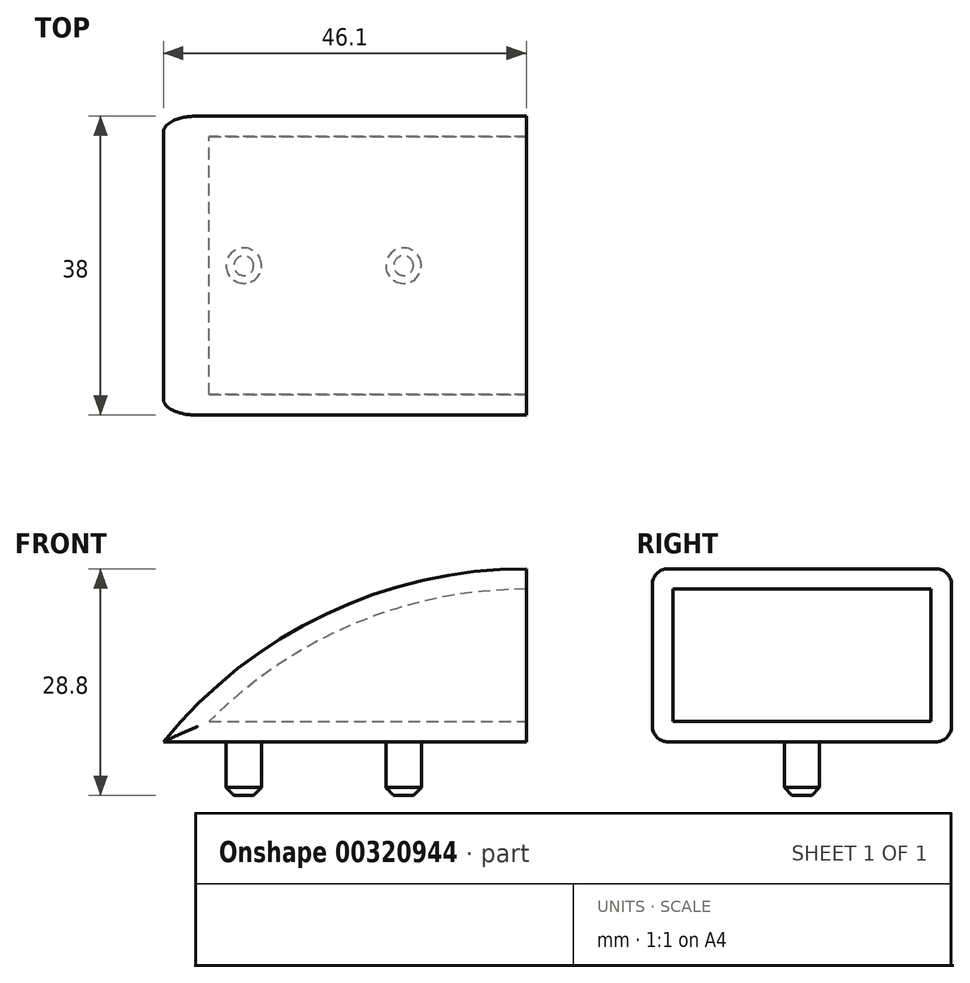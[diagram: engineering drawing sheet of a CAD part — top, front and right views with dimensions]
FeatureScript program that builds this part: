
annotation { "Feature Type Name" : "Feature", "Feature Type Description" : "" }
export const myFeature = defineFeature(function(context is Context, id is Id, definition is map)
    precondition{}
    {
        {
            var Q0;
            Q0=qCreatedBy(makeId("Front.planeOp"),FACE);
            var sketch = newSketch(context, id + "F0", { "sketchPlane" : qUnion([Q0])});
            skLineSegment(sketch, "E0", {"start": v(0, 0) * mm, "end": v(46.1, 0) * mm});
            skLineSegment(sketch, "E1", {"start": v(46.1, 0) * mm, "end": v(46.1, 22) * mm});
            skArc(sketch, "E2", {"start": v(46.1, 22) * mm, "mid": v(20.56, 16.22) * mm, "end": v(0, 0) * mm});
            skSolve(sketch);
        }
        {
            var Q0;
            Q0 = qSketchRegion(id + "F0", true);
            extrude(context, id + "F1", {"entities" : qUnion([Q0]), "depth" : 38 * mm});
        }
        {
            var Q0;
            Q0=makeQuery(id+"F1.opExtrude","SWEPT_FACE",FACE,{"disambiguationData":[OSD([sQuery(id+"F0.wireOp",EDGE,"E1")])]});
            shell(context, id + "F2", {"entities" : qUnion([Q0]), "thickness" : 2.6 * mm});
        }
        {
            var Q0;
            Q0=makeQuery(id+"F1.opExtrude","CAP_EDGE",EDGE,{"disambiguationData":[OSD([sQuery(id+"F0.wireOp",EDGE,"E2")])],"isStart":false});
            var Q1;
            Q1=makeQuery(id+"F1.opExtrude","CAP_EDGE",EDGE,{"disambiguationData":[OSD([sQuery(id+"F0.wireOp",EDGE,"E2")])],"isStart":true});
            var Q2;
            Q2=makeQuery(id+"F1.opExtrude","CAP_EDGE",EDGE,{"disambiguationData":[OSD([sQuery(id+"F0.wireOp",EDGE,"E0")])],"isStart":true});
            var Q3;
            Q3=makeQuery(id+"F1.opExtrude","CAP_EDGE",EDGE,{"disambiguationData":[OSD([sQuery(id+"F0.wireOp",EDGE,"E0")])],"isStart":false});
            fillet(context, id + "F3", {"entities" : qUnion([Q0, Q1, Q2, Q3]), "radius" : 2 * mm, "tangentPropagation" : true, "allowEdgeOverflow" : false});
        }
        {
            var Q0;
            Q0=makeQuery(id+"F1.opExtrude","SWEPT_FACE",FACE,{"disambiguationData":[OSD([sQuery(id+"F0.wireOp",EDGE,"E0")])]});
            var sketch = newSketch(context, id + "F4", { "sketchPlane" : qUnion([Q0])});
            skCircle(sketch, "E3", {"center": v(10.2, 19) * mm, "radius": 2.25 * mm});
            skCircle(sketch, "E4", {"center": v(30.5, 19) * mm, "radius": 2.25 * mm});
            skLineSegment(sketch, "E5", {"start": v(0, 19) * mm, "end": v(46.1, 19) * mm});
            skSolve(sketch);
        }
        {
            var Q0;
            Q0 = qSketchRegion(id + "F4", true);
            extrude(context, id + "F5", {"entities" : qUnion([Q0]), "operationType" : NewBodyOperationType.ADD, "depth" : 6.8 * mm});
        }
        {
            var Q0;
            Q0=makeQuery(id+"F5.opExtrude","CAP_EDGE",EDGE,{"disambiguationData":[OSD([sQuery(id+"F4.wireOp",EDGE,"E3")])],"isStart":false});
            var Q1;
            Q1=makeQuery(id+"F5.opExtrude","CAP_EDGE",EDGE,{"disambiguationData":[OSD([sQuery(id+"F4.wireOp",EDGE,"E4")])],"isStart":false});
            chamfer(context, id + "F6", {"entities" : qUnion([Q0, Q1]), "width" : 1 * mm, "tangentPropagation" : true});
        }
    });
